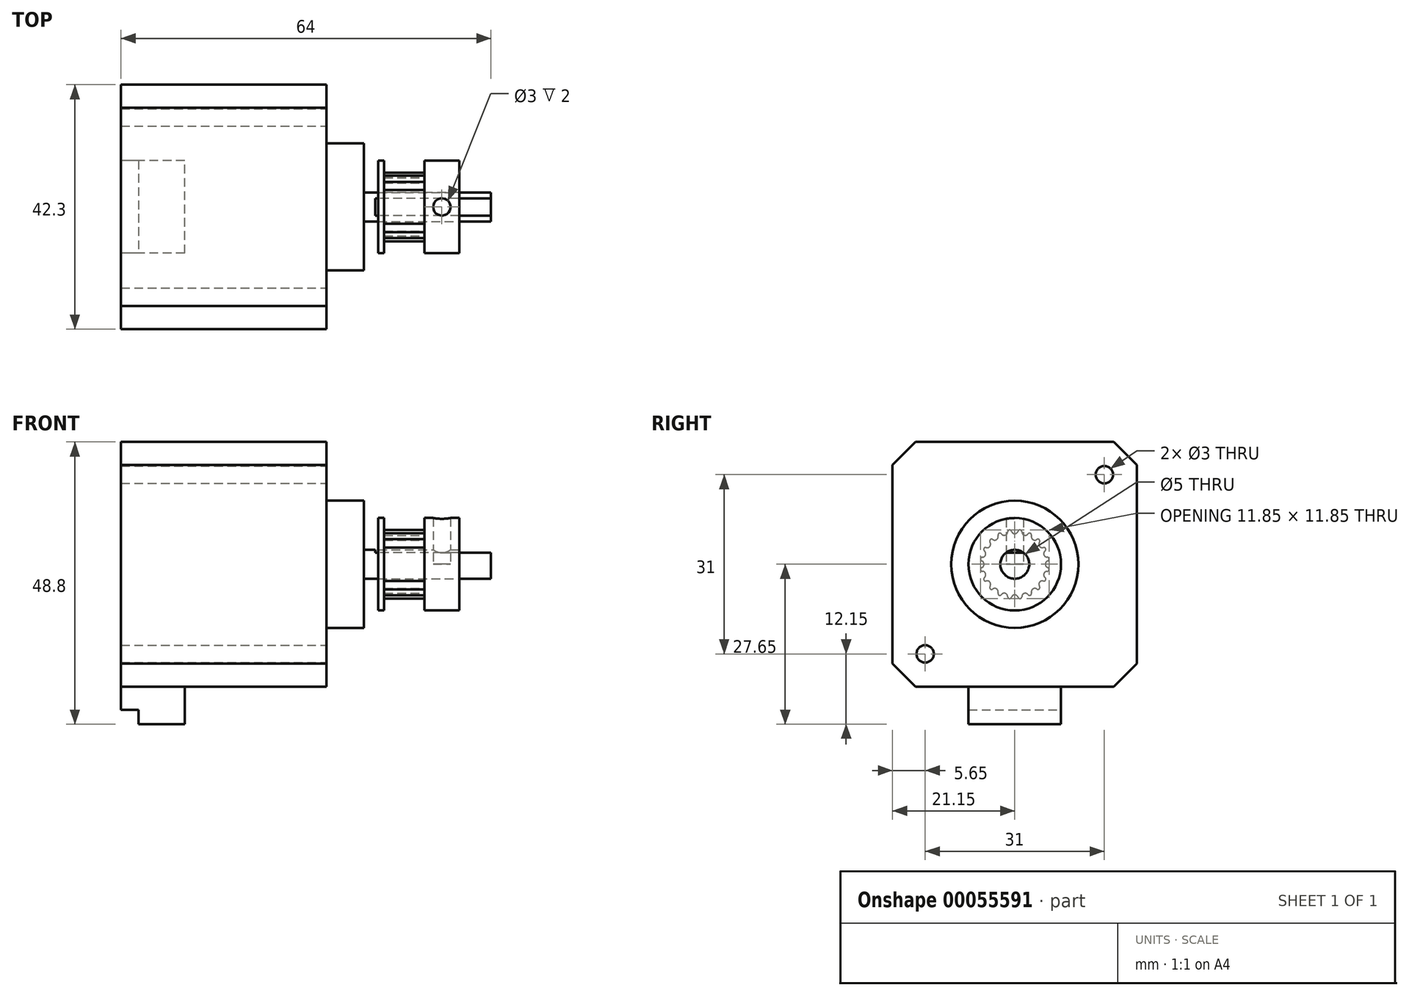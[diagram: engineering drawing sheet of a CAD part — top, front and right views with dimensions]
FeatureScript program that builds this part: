
annotation { "Feature Type Name" : "Feature", "Feature Type Description" : "" }
export const myFeature = defineFeature(function(context is Context, id is Id, definition is map)
    precondition{}
    {
        {
            var Q0;
            Q0=qCreatedBy(makeId("Right.planeOp"),FACE);
            var sketch = newSketch(context, id + "F0", { "sketchPlane" : qUnion([Q0]), "asVersion" : FeatureScriptVersionNumber.V275_SKETCH_PATTERN_LOWER_LIMIT});
            skLineSegment(sketch, "E0", {"start": v(0, 0) * mm, "end": v(-19.15, 19.15) * mm, "construction": true});
            skLineSegment(sketch, "E1", {"start": v(-19.15, 19.15) * mm, "end": v(-17.15, 21.15) * mm});
            skLineSegment(sketch, "E2", {"start": v(-17.15, 21.15) * mm, "end": v(0, 21.15) * mm});
            skCircle(sketch, "E3", {"center": v(-15.5, 15.5) * mm, "radius": 1.5 * mm});
            skLineSegment(sketch, "E4.MirrorCS", {"start": v(-19.15, 19.15) * mm, "end": v(-21.15, 17.15) * mm});
            skLineSegment(sketch, "E5.MirrorCS", {"start": v(-21.15, 17.15) * mm, "end": v(-21.15, 0) * mm});
            skLineSegment(sketch, "E6.MirrorCS", {"start": v(17.15, 21.15) * mm, "end": v(0, 21.15) * mm});
            skCircle(sketch, "E7.MirrorC", {"center": v(15.5, 15.5) * mm, "radius": 1.5 * mm});
            skLineSegment(sketch, "E8.MirrorCS", {"start": v(19.15, 19.15) * mm, "end": v(17.15, 21.15) * mm});
            skLineSegment(sketch, "E9.MirrorCS", {"start": v(19.15, 19.15) * mm, "end": v(21.15, 17.15) * mm});
            skLineSegment(sketch, "E10.MirrorCS", {"start": v(21.15, 17.15) * mm, "end": v(21.15, 0) * mm});
            skLineSegment(sketch, "E11.MirrorCS", {"start": v(-21.15, -17.15) * mm, "end": v(-21.15, 0) * mm});
            skLineSegment(sketch, "E12.MirrorCS", {"start": v(-19.15, -19.15) * mm, "end": v(-21.15, -17.15) * mm});
            skLineSegment(sketch, "E13.MirrorCS", {"start": v(-19.15, -19.15) * mm, "end": v(-17.15, -21.15) * mm});
            skCircle(sketch, "E14.MirrorC", {"center": v(-15.5, -15.5) * mm, "radius": 1.5 * mm});
            skLineSegment(sketch, "E15.MirrorCS", {"start": v(-17.15, -21.15) * mm, "end": v(0, -21.15) * mm});
            skLineSegment(sketch, "E16.MirrorCS", {"start": v(17.15, -21.15) * mm, "end": v(0, -21.15) * mm});
            skLineSegment(sketch, "E17.MirrorCS", {"start": v(19.15, -19.15) * mm, "end": v(17.15, -21.15) * mm});
            skCircle(sketch, "E18.MirrorC", {"center": v(15.5, -15.5) * mm, "radius": 1.5 * mm});
            skLineSegment(sketch, "E19.MirrorCS", {"start": v(19.15, -19.15) * mm, "end": v(21.15, -17.15) * mm});
            skLineSegment(sketch, "E20.MirrorCS", {"start": v(21.15, -17.15) * mm, "end": v(21.15, 0) * mm});
            skCircle(sketch, "E21", {"center": v(0, 0) * mm, "radius": 11 * mm});
            skCircle(sketch, "E22", {"center": v(0, 0) * mm, "radius": 2.5 * mm});
            skLineSegment(sketch, "E23", {"start": v(-1.5, 2) * mm, "end": v(1.5, 2) * mm});
            skSolve(sketch);
        }
        {
            var Q0;
            {var subQ0=sQuery(id+"F0.wireOp",EDGE,"E23");Q0=makeQuery(id+"F0.imprint","IMPRINT",FACE,{"disambiguationData":[TD([[makeQuery(id+"F0.imprint","IMPRINT",EDGE,{"derivedFrom":subQ0}),1.0]])]});}
            var Q1;
            {var subQ0=sQuery(id+"F0.wireOp",EDGE,"E23");Q1=makeQuery(id+"F0.imprint","IMPRINT",FACE,{"disambiguationData":[TD([[makeQuery(id+"F0.imprint","IMPRINT",EDGE,{"derivedFrom":subQ0}),-1.0]])]});}
            var Q2;
            Q2=makeQuery(id+"F0.imprint","IMPRINT",FACE,{"disambiguationData":[TD([[makeQuery(id+"F0.imprint","IMPRINT",EDGE,{"derivedFrom":sQuery(id+"F0.wireOp",EDGE,"E21")}),1.0]])]});
            var Q3;
            Q3=makeQuery(id+"F0.imprint","IMPRINT",FACE,{"disambiguationData":[TD([[makeQuery(id+"F0.imprint","IMPRINT",EDGE,{"derivedFrom":sQuery(id+"F0.wireOp",EDGE,"E7.MirrorC")}),-1.0]])]});
            var Q4;
            Q4=makeQuery(id+"F0.imprint","IMPRINT",FACE,{"disambiguationData":[TD([[makeQuery(id+"F0.imprint","IMPRINT",EDGE,{"derivedFrom":sQuery(id+"F0.wireOp",EDGE,"E18.MirrorC")}),1.0]])]});
            var Q5;
            Q5=makeQuery(id+"F0.imprint","IMPRINT",FACE,{"disambiguationData":[TD([[makeQuery(id+"F0.imprint","IMPRINT",EDGE,{"derivedFrom":sQuery(id+"F0.wireOp",EDGE,"E14.MirrorC")}),-1.0]])]});
            var Q6;
            Q6=makeQuery(id+"F0.imprint","IMPRINT",FACE,{"disambiguationData":[TD([[makeQuery(id+"F0.imprint","IMPRINT",EDGE,{"derivedFrom":sQuery(id+"F0.wireOp",EDGE,"E3")}),1.0]])]});
            var Q7;
            Q7=makeQuery(id+"F0.imprint","IMPRINT",FACE,{"disambiguationData":[TD([[makeQuery(id+"F0.imprint","IMPRINT",EDGE,{"derivedFrom":sQuery(id+"F0.wireOp",EDGE,"E1")}),-1.0]])]});
            extrude(context, id + "F1", {"entities" : qUnion([Q0, Q1, Q2, Q3, Q4, Q5, Q6, Q7]), "oppositeDirection" : true, "depth" : 40 * mm});
        }
        {
            var Q0;
            {var subQ0=sQuery(id+"F0.wireOp",EDGE,"E23");Q0=makeQuery(id+"F0.imprint","IMPRINT",FACE,{"disambiguationData":[TD([[makeQuery(id+"F0.imprint","IMPRINT",EDGE,{"derivedFrom":subQ0}),-1.0]])]});}
            extrude(context, id + "F2", {"entities" : qUnion([Q0]), "operationType" : NewBodyOperationType.ADD, "depth" : 24 * mm});
        }
        {
            var Q0;
            {var subQ0=sQuery(id+"F0.wireOp",EDGE,"E23");Q0=makeQuery(id+"F0.imprint","IMPRINT",FACE,{"disambiguationData":[TD([[makeQuery(id+"F0.imprint","IMPRINT",EDGE,{"derivedFrom":subQ0}),1.0]])]});}
            extrude(context, id + "F3", {"entities" : qUnion([Q0]), "operationType" : NewBodyOperationType.ADD, "depth" : 4 * mm});
        }
        {
            var Q0;
            Q0=makeQuery(id+"F0.imprint","IMPRINT",FACE,{"disambiguationData":[TD([[makeQuery(id+"F0.imprint","IMPRINT",EDGE,{"derivedFrom":sQuery(id+"F0.wireOp",EDGE,"E21")}),1.0]])]});
            extrude(context, id + "F4", {"entities" : qUnion([Q0]), "operationType" : NewBodyOperationType.ADD, "depth" : 2 * mm});
        }
        {
            var Q0;
            Q0=makeQuery(id+"F0.imprint","IMPRINT",FACE,{"disambiguationData":[TD([[makeQuery(id+"F0.imprint","IMPRINT",EDGE,{"derivedFrom":sQuery(id+"F0.wireOp",EDGE,"E3")}),1.0]])]});
            var Q1;
            Q1=makeQuery(id+"F0.imprint","IMPRINT",FACE,{"disambiguationData":[TD([[makeQuery(id+"F0.imprint","IMPRINT",EDGE,{"derivedFrom":sQuery(id+"F0.wireOp",EDGE,"E7.MirrorC")}),-1.0]])]});
            var Q2;
            Q2=makeQuery(id+"F0.imprint","IMPRINT",FACE,{"disambiguationData":[TD([[makeQuery(id+"F0.imprint","IMPRINT",EDGE,{"derivedFrom":sQuery(id+"F0.wireOp",EDGE,"E18.MirrorC")}),1.0]])]});
            var Q3;
            Q3=makeQuery(id+"F0.imprint","IMPRINT",FACE,{"disambiguationData":[TD([[makeQuery(id+"F0.imprint","IMPRINT",EDGE,{"derivedFrom":sQuery(id+"F0.wireOp",EDGE,"E14.MirrorC")}),-1.0]])]});
            extrude(context, id + "F5", {"entities" : qUnion([Q0, Q1, Q2, Q3]), "operationType" : NewBodyOperationType.REMOVE, "oppositeDirection" : true, "depth" : 4.5 * mm});
        }
        {
            var Q0;
            Q0=makeQuery(id+"F1.opExtrude","CAP_FACE",FACE,{"disambiguationData":[OSD([sQuery(id+"F0.wireOp",EDGE,"E1"),sQuery(id+"F0.wireOp",EDGE,"E2"),sQuery(id+"F0.wireOp",EDGE,"E4.MirrorCS"),sQuery(id+"F0.wireOp",EDGE,"E5.MirrorCS"),sQuery(id+"F0.wireOp",EDGE,"E6.MirrorCS"),sQuery(id+"F0.wireOp",EDGE,"E8.MirrorCS"),sQuery(id+"F0.wireOp",EDGE,"E9.MirrorCS"),sQuery(id+"F0.wireOp",EDGE,"E10.MirrorCS"),sQuery(id+"F0.wireOp",EDGE,"E11.MirrorCS"),sQuery(id+"F0.wireOp",EDGE,"E12.MirrorCS"),sQuery(id+"F0.wireOp",EDGE,"E13.MirrorCS"),sQuery(id+"F0.wireOp",EDGE,"E15.MirrorCS"),sQuery(id+"F0.wireOp",EDGE,"E16.MirrorCS"),sQuery(id+"F0.wireOp",EDGE,"E17.MirrorCS"),sQuery(id+"F0.wireOp",EDGE,"E19.MirrorCS"),sQuery(id+"F0.wireOp",EDGE,"E20.MirrorCS")])],"isStart":false});
            var sketch = newSketch(context, id + "F6", { "sketchPlane" : qUnion([Q0]), "asVersion" : FeatureScriptVersionNumber.V275_SKETCH_PATTERN_LOWER_LIMIT});
            skLineSegment(sketch, "E24", {"start": v(-8, -21.15) * mm, "end": v(-8, -27.65) * mm});
            skLineSegment(sketch, "E25.MirrorCS", {"start": v(8, -21.15) * mm, "end": v(8, -27.65) * mm});
            skLineSegment(sketch, "E26", {"start": v(-8, -27.65) * mm, "end": v(8, -27.65) * mm});
            skLineSegment(sketch, "E27", {"start": v(-8, -21.15) * mm, "end": v(8, -21.15) * mm});
            skLineSegment(sketch, "E28", {"start": v(8, -25.15) * mm, "end": v(-8, -25.15) * mm});
            skSolve(sketch);
        }
        {
            var Q0;
            {var subQ0=sQuery(id+"F6.wireOp",EDGE,"E27");Q0=makeQuery(id+"F6.imprint","IMPRINT",FACE,{"disambiguationData":[TD([[makeQuery(id+"F6.imprint","IMPRINT",EDGE,{"derivedFrom":subQ0}),1.0]])]});}
            var Q1;
            {var subQ1=sQuery(id+"F6.wireOp",EDGE,"E26");Q1=makeQuery(id+"F6.imprint","IMPRINT",FACE,{"disambiguationData":[TD([[makeQuery(id+"F6.imprint","IMPRINT",EDGE,{"derivedFrom":subQ1}),1.0]])]});}
            extrude(context, id + "F7", {"entities" : qUnion([Q0, Q1]), "operationType" : NewBodyOperationType.ADD, "oppositeDirection" : true, "depth" : 11 * mm});
        }
        {
            var Q0;
            {var subQ1=sQuery(id+"F6.wireOp",EDGE,"E26");Q0=makeQuery(id+"F6.imprint","IMPRINT",FACE,{"disambiguationData":[TD([[makeQuery(id+"F6.imprint","IMPRINT",EDGE,{"derivedFrom":subQ1}),1.0]])]});}
            extrude(context, id + "F8", {"entities" : qUnion([Q0]), "operationType" : NewBodyOperationType.REMOVE, "oppositeDirection" : true, "depth" : 3 * mm});
        }
        {
            var Q0;
            Q0=qCreatedBy(makeId("Right.planeOp"),FACE);
            cPlane(context, id + "F9", {"entities" : qUnion([Q0]), "cplaneType" : CPlaneType.OFFSET, "offset" : 9 * mm, "width" : 150 * mm, "height" : 150 * mm});
        }
        {
            var Q0;
            Q0=qCreatedBy(id+"F9.planeOp",FACE);
            var sketch = newSketch(context, id + "F10", { "sketchPlane" : qUnion([Q0]), "asVersion" : FeatureScriptVersionNumber.V275_SKETCH_PATTERN_LOWER_LIMIT});
            skCircle(sketch, "E29", {"center": v(0, 0) * mm, "radius": 8 * mm});
            skCircle(sketch, "E30", {"center": v(0, 0) * mm, "radius": 2.5 * mm});
            skSolve(sketch);
        }
        {
            var Q0;
            Q0=makeQuery(id+"F10.imprint","IMPRINT",FACE,{"disambiguationData":[TD([[makeQuery(id+"F10.imprint","IMPRINT",EDGE,{"derivedFrom":sQuery(id+"F10.wireOp",EDGE,"E29")}),1.0]])]});
            extrude(context, id + "F11", {"entities" : qUnion([Q0]), "oppositeDirection" : true, "depth" : 4.5 * mm, "hasSecondDirection" : true, "secondDirectionOppositeDirection" : false, "secondDirectionDepth" : 9.5 * mm});
        }
        {
            var Q0;
            Q0=qCreatedBy(id+"F9.planeOp",FACE);
            var sketch = newSketch(context, id + "F12", { "sketchPlane" : qUnion([Q0]), "asVersion" : FeatureScriptVersionNumber.V275_SKETCH_PATTERN_LOWER_LIMIT});
            skArc(sketch, "E31", {"start": v(-0.57, 5.7) * mm, "mid": v(0, 5.3) * mm, "end": v(0.57, 5.7) * mm});
            skArc(sketch, "E32", {"start": v(0.94, 5.93) * mm, "mid": v(0.71, 5.88) * mm, "end": v(0.57, 5.7) * mm});
            skLineSegment(sketch, "E33", {"start": v(0, 5.9) * mm, "end": v(0, 0) * mm, "construction": true});
            skLineSegment(sketch, "E34", {"start": v(0, 0) * mm, "end": v(0.94, 5.93) * mm, "construction": true});
            skArc(sketch, "E35.MirrorCS", {"start": v(-0.94, 5.93) * mm, "mid": v(-0.71, 5.88) * mm, "end": v(-0.57, 5.7) * mm});
            skArc(sketch, "E36.1.0", {"start": v(2.72, 5.35) * mm, "mid": v(2.5, 5.37) * mm, "end": v(2.3, 5.25) * mm});
            skArc(sketch, "E36.1.1", {"start": v(1.22, 5.6) * mm, "mid": v(1.64, 5.04) * mm, "end": v(2.3, 5.25) * mm});
            skArc(sketch, "E36.1.2", {"start": v(0.94, 5.93) * mm, "mid": v(1.14, 5.81) * mm, "end": v(1.22, 5.6) * mm});
            skArc(sketch, "E36.2.0", {"start": v(4.24, 4.24) * mm, "mid": v(4.03, 4.34) * mm, "end": v(3.81, 4.28) * mm});
            skArc(sketch, "E36.2.1", {"start": v(2.9, 4.95) * mm, "mid": v(3.12, 4.29) * mm, "end": v(3.81, 4.28) * mm});
            skArc(sketch, "E36.2.2", {"start": v(2.72, 5.35) * mm, "mid": v(2.88, 5.18) * mm, "end": v(2.9, 4.95) * mm});
            skArc(sketch, "E36.3.0", {"start": v(5.35, 2.72) * mm, "mid": v(5.18, 2.88) * mm, "end": v(4.95, 2.9) * mm});
            skArc(sketch, "E36.3.1", {"start": v(4.28, 3.81) * mm, "mid": v(4.29, 3.12) * mm, "end": v(4.95, 2.9) * mm});
            skArc(sketch, "E36.3.2", {"start": v(4.24, 4.24) * mm, "mid": v(4.34, 4.03) * mm, "end": v(4.28, 3.81) * mm});
            skArc(sketch, "E36.4.0", {"start": v(5.93, 0.94) * mm, "mid": v(5.81, 1.14) * mm, "end": v(5.6, 1.22) * mm});
            skArc(sketch, "E36.4.1", {"start": v(5.25, 2.3) * mm, "mid": v(5.04, 1.64) * mm, "end": v(5.6, 1.22) * mm});
            skArc(sketch, "E36.4.2", {"start": v(5.35, 2.72) * mm, "mid": v(5.37, 2.5) * mm, "end": v(5.25, 2.3) * mm});
            skArc(sketch, "E36.5.0", {"start": v(5.93, -0.94) * mm, "mid": v(5.88, -0.71) * mm, "end": v(5.7, -0.57) * mm});
            skArc(sketch, "E36.5.1", {"start": v(5.7, 0.57) * mm, "mid": v(5.3, 0) * mm, "end": v(5.7, -0.57) * mm});
            skArc(sketch, "E36.5.2", {"start": v(5.93, 0.94) * mm, "mid": v(5.88, 0.71) * mm, "end": v(5.7, 0.57) * mm});
            skArc(sketch, "E36.6.0", {"start": v(5.35, -2.72) * mm, "mid": v(5.37, -2.5) * mm, "end": v(5.25, -2.3) * mm});
            skArc(sketch, "E36.6.1", {"start": v(5.6, -1.22) * mm, "mid": v(5.04, -1.64) * mm, "end": v(5.25, -2.3) * mm});
            skArc(sketch, "E36.6.2", {"start": v(5.93, -0.94) * mm, "mid": v(5.81, -1.14) * mm, "end": v(5.6, -1.22) * mm});
            skArc(sketch, "E36.7.0", {"start": v(4.24, -4.24) * mm, "mid": v(4.34, -4.03) * mm, "end": v(4.28, -3.81) * mm});
            skArc(sketch, "E36.7.1", {"start": v(4.95, -2.9) * mm, "mid": v(4.29, -3.12) * mm, "end": v(4.28, -3.81) * mm});
            skArc(sketch, "E36.7.2", {"start": v(5.35, -2.72) * mm, "mid": v(5.18, -2.88) * mm, "end": v(4.95, -2.9) * mm});
            skArc(sketch, "E36.8.0", {"start": v(2.72, -5.35) * mm, "mid": v(2.88, -5.18) * mm, "end": v(2.9, -4.95) * mm});
            skArc(sketch, "E36.8.1", {"start": v(3.81, -4.28) * mm, "mid": v(3.12, -4.29) * mm, "end": v(2.9, -4.95) * mm});
            skArc(sketch, "E36.8.2", {"start": v(4.24, -4.24) * mm, "mid": v(4.03, -4.34) * mm, "end": v(3.81, -4.28) * mm});
            skArc(sketch, "E36.9.0", {"start": v(0.94, -5.93) * mm, "mid": v(1.14, -5.81) * mm, "end": v(1.22, -5.6) * mm});
            skArc(sketch, "E36.9.1", {"start": v(2.3, -5.25) * mm, "mid": v(1.64, -5.04) * mm, "end": v(1.22, -5.6) * mm});
            skArc(sketch, "E36.9.2", {"start": v(2.72, -5.35) * mm, "mid": v(2.5, -5.37) * mm, "end": v(2.3, -5.25) * mm});
            skArc(sketch, "E36.10.0", {"start": v(-0.94, -5.93) * mm, "mid": v(-0.71, -5.88) * mm, "end": v(-0.57, -5.7) * mm});
            skArc(sketch, "E36.10.1", {"start": v(0.57, -5.7) * mm, "mid": v(0, -5.3) * mm, "end": v(-0.57, -5.7) * mm});
            skArc(sketch, "E36.10.2", {"start": v(0.94, -5.93) * mm, "mid": v(0.71, -5.88) * mm, "end": v(0.57, -5.7) * mm});
            skArc(sketch, "E36.11.0", {"start": v(-2.72, -5.35) * mm, "mid": v(-2.5, -5.37) * mm, "end": v(-2.3, -5.25) * mm});
            skArc(sketch, "E36.11.1", {"start": v(-1.22, -5.6) * mm, "mid": v(-1.64, -5.04) * mm, "end": v(-2.3, -5.25) * mm});
            skArc(sketch, "E36.11.2", {"start": v(-0.94, -5.93) * mm, "mid": v(-1.14, -5.81) * mm, "end": v(-1.22, -5.6) * mm});
            skArc(sketch, "E36.12.0", {"start": v(-4.24, -4.24) * mm, "mid": v(-4.03, -4.34) * mm, "end": v(-3.81, -4.28) * mm});
            skArc(sketch, "E36.12.1", {"start": v(-2.9, -4.95) * mm, "mid": v(-3.12, -4.29) * mm, "end": v(-3.81, -4.28) * mm});
            skArc(sketch, "E36.12.2", {"start": v(-2.72, -5.35) * mm, "mid": v(-2.88, -5.18) * mm, "end": v(-2.9, -4.95) * mm});
            skArc(sketch, "E36.13.0", {"start": v(-5.35, -2.72) * mm, "mid": v(-5.18, -2.88) * mm, "end": v(-4.95, -2.9) * mm});
            skArc(sketch, "E36.13.1", {"start": v(-4.28, -3.81) * mm, "mid": v(-4.29, -3.12) * mm, "end": v(-4.95, -2.9) * mm});
            skArc(sketch, "E36.13.2", {"start": v(-4.24, -4.24) * mm, "mid": v(-4.34, -4.03) * mm, "end": v(-4.28, -3.81) * mm});
            skArc(sketch, "E36.14.0", {"start": v(-5.93, -0.94) * mm, "mid": v(-5.81, -1.14) * mm, "end": v(-5.6, -1.22) * mm});
            skArc(sketch, "E36.14.1", {"start": v(-5.25, -2.3) * mm, "mid": v(-5.04, -1.64) * mm, "end": v(-5.6, -1.22) * mm});
            skArc(sketch, "E36.14.2", {"start": v(-5.35, -2.72) * mm, "mid": v(-5.37, -2.5) * mm, "end": v(-5.25, -2.3) * mm});
            skArc(sketch, "E36.15.0", {"start": v(-5.93, 0.94) * mm, "mid": v(-5.88, 0.71) * mm, "end": v(-5.7, 0.57) * mm});
            skArc(sketch, "E36.15.1", {"start": v(-5.7, -0.57) * mm, "mid": v(-5.3, 0) * mm, "end": v(-5.7, 0.57) * mm});
            skArc(sketch, "E36.15.2", {"start": v(-5.93, -0.94) * mm, "mid": v(-5.88, -0.71) * mm, "end": v(-5.7, -0.57) * mm});
            skArc(sketch, "E36.16.0", {"start": v(-5.35, 2.72) * mm, "mid": v(-5.37, 2.5) * mm, "end": v(-5.25, 2.3) * mm});
            skArc(sketch, "E36.16.1", {"start": v(-5.6, 1.22) * mm, "mid": v(-5.04, 1.64) * mm, "end": v(-5.25, 2.3) * mm});
            skArc(sketch, "E36.16.2", {"start": v(-5.93, 0.94) * mm, "mid": v(-5.81, 1.14) * mm, "end": v(-5.6, 1.22) * mm});
            skArc(sketch, "E36.17.0", {"start": v(-4.24, 4.24) * mm, "mid": v(-4.34, 4.03) * mm, "end": v(-4.28, 3.81) * mm});
            skArc(sketch, "E36.17.1", {"start": v(-4.95, 2.9) * mm, "mid": v(-4.29, 3.12) * mm, "end": v(-4.28, 3.81) * mm});
            skArc(sketch, "E36.17.2", {"start": v(-5.35, 2.72) * mm, "mid": v(-5.18, 2.88) * mm, "end": v(-4.95, 2.9) * mm});
            skArc(sketch, "E36.18.0", {"start": v(-2.72, 5.35) * mm, "mid": v(-2.88, 5.18) * mm, "end": v(-2.9, 4.95) * mm});
            skArc(sketch, "E36.18.1", {"start": v(-3.81, 4.28) * mm, "mid": v(-3.12, 4.29) * mm, "end": v(-2.9, 4.95) * mm});
            skArc(sketch, "E36.18.2", {"start": v(-4.24, 4.24) * mm, "mid": v(-4.03, 4.34) * mm, "end": v(-3.81, 4.28) * mm});
            skArc(sketch, "E36.19.0", {"start": v(-0.94, 5.93) * mm, "mid": v(-1.14, 5.81) * mm, "end": v(-1.22, 5.6) * mm});
            skArc(sketch, "E36.19.1", {"start": v(-2.3, 5.25) * mm, "mid": v(-1.64, 5.04) * mm, "end": v(-1.22, 5.6) * mm});
            skArc(sketch, "E36.19.2", {"start": v(-2.72, 5.35) * mm, "mid": v(-2.5, 5.37) * mm, "end": v(-2.3, 5.25) * mm});
            skPoint(sketch, "E36.center", {"position": v(0, 0) * mm});
            skLineSegment(sketch, "E36.anchor1", {"start": v(0, 0) * mm, "end": v(0.57, 5.7) * mm, "construction": true});
            skLineSegment(sketch, "E36.anchor2", {"start": v(0, 0) * mm, "end": v(-1.22, 5.6) * mm, "construction": true});
            skCircle(sketch, "E37", {"center": v(0, 0) * mm, "radius": 8 * mm});
            skSolve(sketch);
        }
        {
            var Q0;
            Q0=makeQuery(id+"F12.imprint","IMPRINT",FACE,{"disambiguationData":[TD([[makeQuery(id+"F12.imprint","IMPRINT",EDGE,{"derivedFrom":sQuery(id+"F12.wireOp",EDGE,"E31")}),1.0]])]});
            extrude(context, id + "F13", {"entities" : qUnion([Q0]), "operationType" : NewBodyOperationType.REMOVE, "endBound" : BoundingType.SYMMETRIC, "oppositeDirection" : true, "depth" : 7 * mm});
        }
        {
            var Q0;
            Q0=qCreatedBy(makeId("Top.planeOp"),FACE);
            var sketch = newSketch(context, id + "F14", { "sketchPlane" : qUnion([Q0]), "asVersion" : FeatureScriptVersionNumber.V275_SKETCH_PATTERN_LOWER_LIMIT});
            skCircle(sketch, "E38", {"center": v(15.5, 0) * mm, "radius": 1.5 * mm});
            skSolve(sketch);
        }
        {
            var Q0;
            Q0=makeQuery(id+"F14.imprint","IMPRINT",FACE,{"disambiguationData":[TD([[makeQuery(id+"F14.imprint","IMPRINT",EDGE,{"derivedFrom":sQuery(id+"F14.wireOp",EDGE,"E38")}),1.0]])]});
            extrude(context, id + "F15", {"entities" : qUnion([Q0]), "operationType" : NewBodyOperationType.REMOVE, "depth" : 25 * mm});
        }
    });
